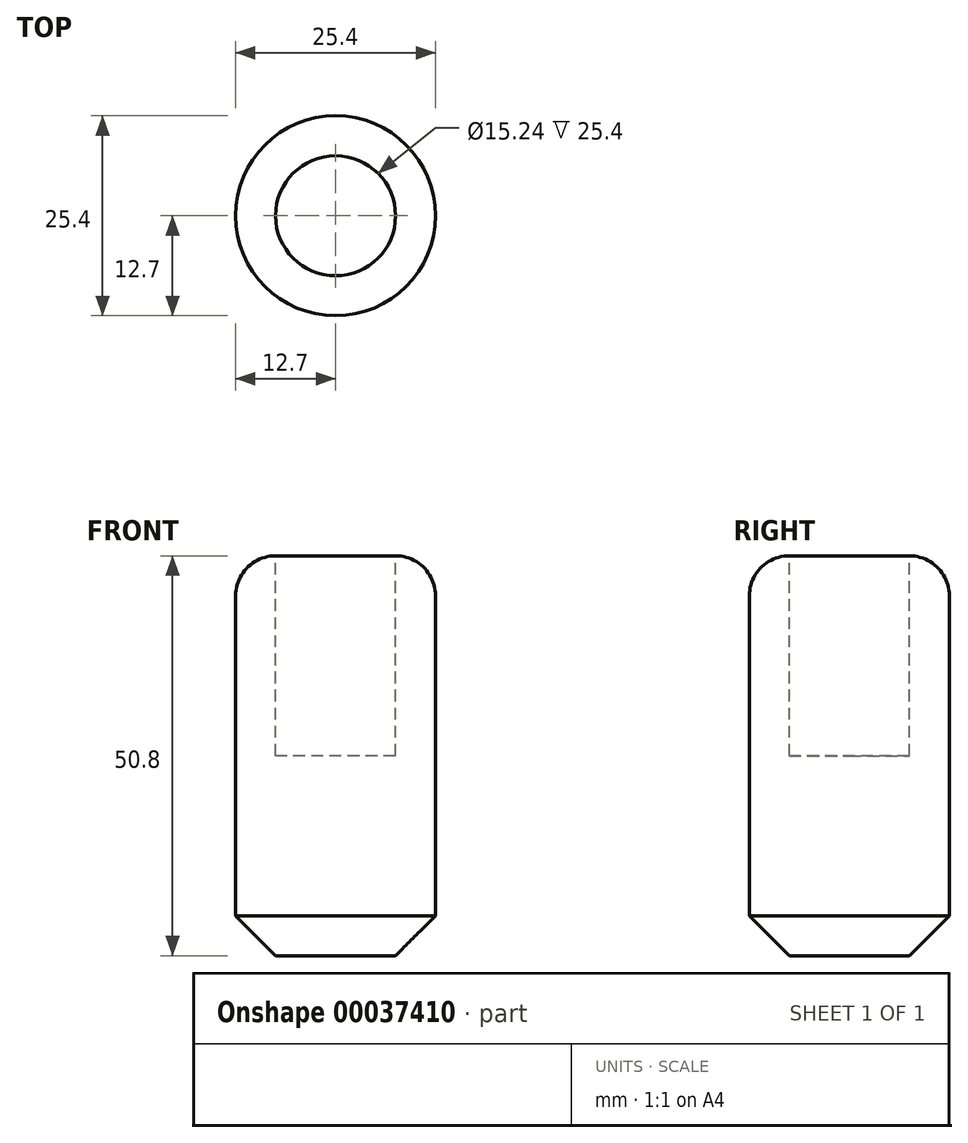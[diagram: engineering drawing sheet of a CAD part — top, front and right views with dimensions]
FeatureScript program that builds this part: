
annotation { "Feature Type Name" : "Feature", "Feature Type Description" : "" }
export const myFeature = defineFeature(function(context is Context, id is Id, definition is map)
    precondition{}
    {
        {
            var Q0;
            Q0=qCreatedBy(makeId("Top.planeOp"),FACE);
            var sketch = newSketch(context, id + "F0", { "sketchPlane" : qUnion([Q0])});
            skCircle(sketch, "E0", {"center": v(0, 0) * mm, "radius": 12.7 * mm});
            skSolve(sketch);
        }
        {
            var Q0;
            Q0 = qSketchRegion(id + "F0", true);
            extrude(context, id + "F1", {"entities" : qUnion([Q0]), "depth" : 50.8 * mm});
        }
        {
            var Q0;
            Q0=makeQuery(id+"F1.opExtrude","CAP_EDGE",EDGE,{"disambiguationData":[OSD([sQuery(id+"F0.wireOp",EDGE,"E0")])],"isStart":false});
            fillet(context, id + "F2", {"entities" : qUnion([Q0]), "radius" : 5.08 * mm, "tangentPropagation" : true, "allowEdgeOverflow" : false});
        }
        {
            var Q0;
            Q0=makeQuery(id+"F1.opExtrude","CAP_EDGE",EDGE,{"disambiguationData":[OSD([sQuery(id+"F0.wireOp",EDGE,"E0")])],"isStart":true});
            chamfer(context, id + "F3", {"entities" : qUnion([Q0]), "width" : 5.08 * mm, "tangentPropagation" : true});
        }
        {
            var Q0;
            Q0=makeQuery(id+"F1.opExtrude","CAP_FACE",FACE,{"disambiguationData":[OSD([sQuery(id+"F0.wireOp",EDGE,"E0")])],"isStart":false});
            extrude(context, id + "F4", {"entities" : qUnion([Q0]), "operationType" : NewBodyOperationType.REMOVE, "oppositeDirection" : true, "depth" : 25.4 * mm});
        }
    });
